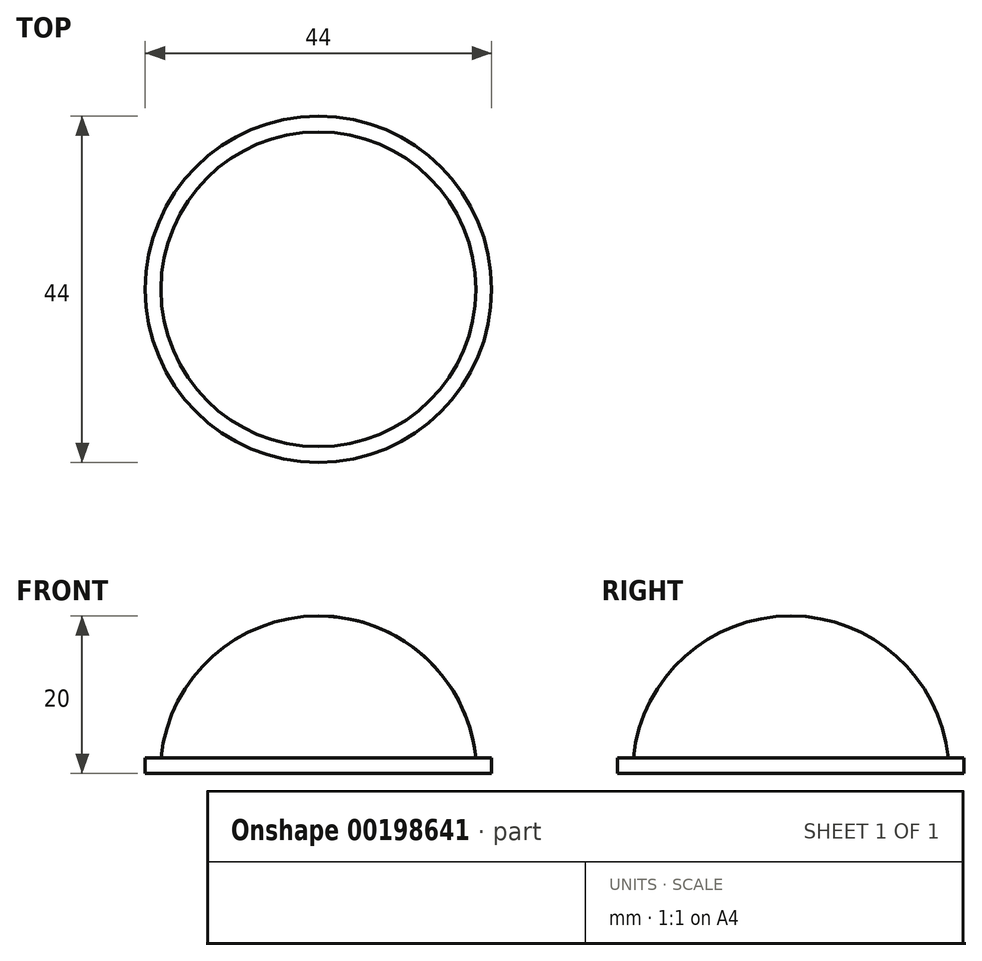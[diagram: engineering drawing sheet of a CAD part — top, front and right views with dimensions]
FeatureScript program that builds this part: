
annotation { "Feature Type Name" : "Feature", "Feature Type Description" : "" }
export const myFeature = defineFeature(function(context is Context, id is Id, definition is map)
    precondition{}
    {
        {
            var Q0;
            Q0=qCreatedBy(makeId("Front.planeOp"),FACE);
            var sketch = newSketch(context, id + "F0", { "sketchPlane" : qUnion([Q0])});
            skLineSegment(sketch, "E0.bottom", {"start": v(-22, 0) * mm, "end": v(22, 0) * mm});
            skLineSegment(sketch, "E0.top", {"start": v(-22, 2) * mm, "end": v(22, 2) * mm});
            skLineSegment(sketch, "E0.left", {"start": v(-22, 0) * mm, "end": v(-22, 2) * mm});
            skLineSegment(sketch, "E0.right", {"start": v(22, 0) * mm, "end": v(22, 2) * mm});
            skPoint(sketch, "E1", {"position": v(-20, 2) * mm});
            skPoint(sketch, "E2", {"position": v(20, 2) * mm});
            skArc(sketch, "E3", {"start": v(20, 2) * mm, "mid": v(0, 20) * mm, "end": v(-20, 2) * mm});
            skLineSegment(sketch, "E4", {"start": v(0, 0) * mm, "end": v(0, 20) * mm});
            skPoint(sketch, "E4.endSnap0", {"position": v(0, 2) * mm});
            skSolve(sketch);
        }
        {
            var Q0;
            {var subQ0=sQuery(id+"F0.wireOp",EDGE,"E3");var subQ1=sQuery(id+"F0.wireOp",EDGE,"E0.top");var subQ2=makeQuery(id+"F0.imprint","INTERSECT",VERTEX,{"disambiguationData":[OD(0.0)],"derivedFrom":[subQ1,subQ0]});Q0=makeQuery(id+"F0.imprint","IMPRINT",FACE,{"disambiguationData":[TD([[makeQuery(id+"F0.imprint","IMPRINT",EDGE,{"disambiguationData":[TD([[subQ2,1.0]])],"derivedFrom":subQ1}),1.0]])]});}
            var Q1;
            {var subQ0=sQuery(id+"F0.wireOp",EDGE,"E0.right");Q1=makeQuery(id+"F0.imprint","IMPRINT",FACE,{"disambiguationData":[TD([[makeQuery(id+"F0.imprint","IMPRINT",EDGE,{"derivedFrom":subQ0}),1.0]])]});}
            var Q2;
            Q2=sQuery(id+"F0.wireOp",EDGE,"E4");
            revolve(context, id + "F1", {"entities" : qUnion([Q0, Q1]), "axis" : qUnion([Q2]), "revolveType" : RevolveType.FULL});
        }
    });
